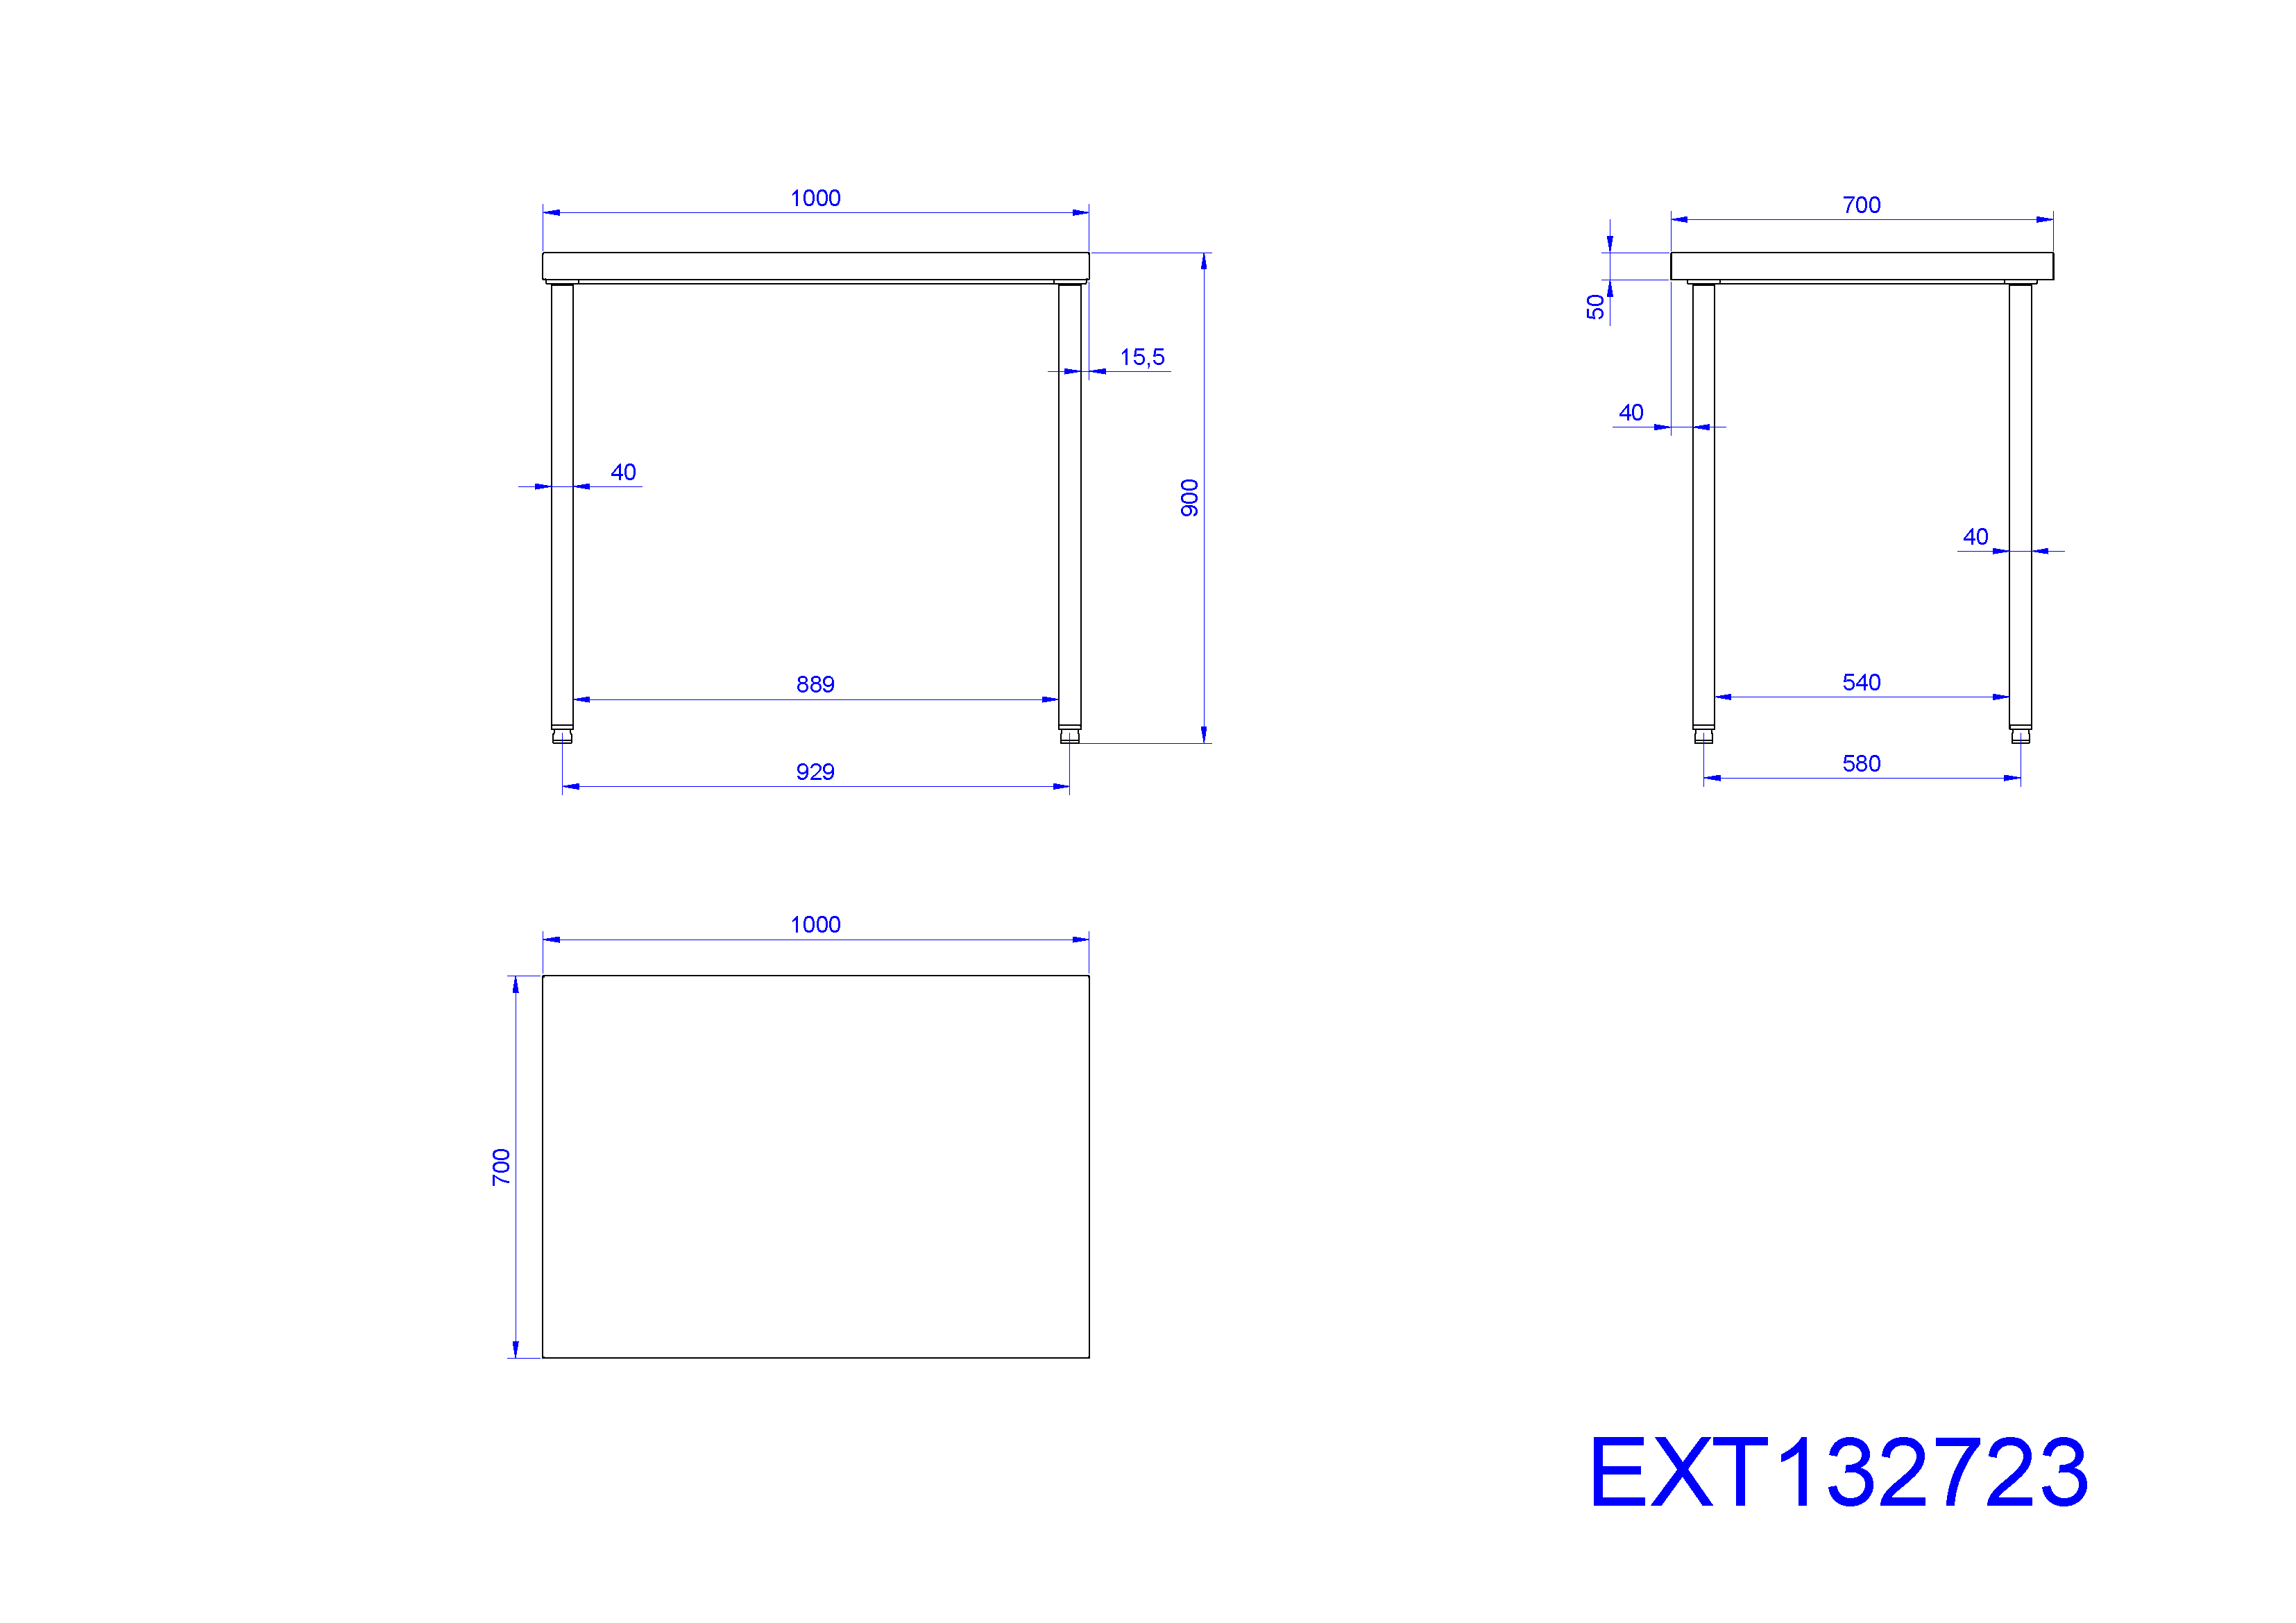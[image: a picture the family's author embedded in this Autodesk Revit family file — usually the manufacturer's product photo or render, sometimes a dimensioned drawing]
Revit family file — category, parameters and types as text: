
# Revit family: QF_ELECTROLUXPROFESSIONAL_132839_WTD1007N
name_source: partatom
category: Attrezzature speciali
units: mm (PartAtom-declared; Revit-internal decimal feet)

## family parameters
Basato su piano di lavoro = No
Condiviso = No
Punto di calcolo locali = No
Quota connettore circolare = Usa diametro
Sempre verticale = Sì
Taglio con vuoti quando caricato = No
Tipo di parte = Normale

## types (1)
- Standard
    Accessory = Sì
    Cold Water Size = 0 mm
    Compressed Air Pressure = 0.0 Pa
    Compressed Air Size = 0 mm
    Compressed Air Volume = 0.0 L/s
    Condensate Return Size = 0 mm
    Cycle = 0 Hz
    Depth Actual = 700 mm  [stored 2.29659 ft]
    Descrizione = WORK TABLE-DISASSEMBLED 1000MM
    Direct Waste Size = 0 mm
    Gas Input Pressure = 0
    Gas KW = 0
    Gas Size = 0 mm
    HP = 0 HP
    Height Actual = 900 mm  [stored 2.95276 ft]
    Hot Water Size = 0 mm
    Item Number = 132839
    Length Actual = 1000 mm  [stored 3.28084 ft]
    Modello = WTD1007N
    Phase = 0
    Produttore = Electrolux Professional
    Prospetto di default = 0 mm  [stored 0 ft]
    Refrigerant Compressor Remote = Sì
    Refrigeration Liquid Line Size = 0 mm  [stored 0 ft]
    Refrigeration Suction Line Size = 0 mm  [stored 0 ft]
    Steam Consumption per Hour = 0
    Steam Supply Maximum Pressure = 0.0 Pa
    Steam Supply Minimum Pressure = 0.0 Pa
    Steam Supply Size = 0 mm
    URL = https://www.electroluxprofessional.com
    URL Manufacturer = https://www.electroluxprofessional.com
    Volts = 0 V
    Watts = 0 W
    Weight = 37.00 kg

note: source unit labels omitted for Gas Input Pressure — the stored unit's dimension contradicts the parameter name (converter mislabeling)

note: [stored X ft] marks values corroborated as IEEE doubles in the binary element streams (Revit-internal decimal feet)

## geometry (parser evidence)
native form markers: Sweep x2
no freeform markers — native parametric forms only
